# Revit family: 36-52-116 DN65-300
name_source: partatom
category: Pipe Accessories
units: mm (PartAtom-declared; Revit-internal decimal feet)

## family parameters
Always vertical = No
Cut with Voids When Loaded = No
Part Type = Valve - Breaks Into
Round Connector Dimension = Use Diameter
Shared = No
Work Plane-Based = No

## types (13) — shared parameters
2 = 2 mm  [stored 0.00656168 ft]
36-075-52-161086 = DN065_D075
36-090-52-16108699 = DN080_D090
36-110-52-16108699 = DN100_D110
36-125-52-16108699 = DN125_D125
36-140-52-16108699 = DN125_D140
36-160-52-16108699 = DN150_D160
36-180-52-16108699 = DN150_D180
36-200-52-16108699 = DN200_D200
36-225-52-16108699 = DN200_D225
36-250-52-161086 = DN250_D250
36-280-52-161086 = DN250_D280
36-315-52-161086 = DN300_D315
36-400-52-161086 = DN300_D355
Description_ = AVK GATE VALVE, PREMIUM 100, PE PIPE ENDS, PN16
Search_table = 36-52-116 DN65-300
Thickness = 9 mm  [stored 0.0295276 ft]
URL product pages = https://www.avkvalves.com
zero-valued in all types: Default Elevation

## per-type parameters (varying)
- DN065_D075: Body_Height=115 mm; Body_L=54.5 mm; Body_Rib_H=57 mm; Body_Rib_L=85 mm; Body_Rib_Start=28 mm; Body_Rib_T=7 mm  [stored 0.0229659 ft]; Body_W=37 mm; Body_dim=26.4 mm; Body_dim3=59.95 mm; Body_dim4=40.7 mm; Body_dimension1=21.6 mm  [stored 0.0708661 ft]; Body_dimension2=39.1 mm; Bonnet_Dim4=29.9 mm; Bonnet_FL_L=67.5 mm; Bonnet_FL_T=8 mm  [stored 0.0262467 ft]; Bonnet_FL_W=50 mm; Bonnet_dim1=62.68 mm; Bonnet_dim2=29.6 mm; Bonnet_dim3=20.72 mm  [stored 0.067979 ft]; Bonnet_dim4=26.64 mm; Bore=32.5 mm; Bottom_revolve=38.15 mm; D=37.5 mm; DN=65 mm; Dd=32.5 mm; F=17 mm  [stored 0.0557743 ft]; F1=20 mm  [stored 0.0656168 ft]; F2=34 mm; FL_T=18 mm  [stored 0.0590551 ft]; Fillet=24 mm; Fillet1=28.8 mm; Fitting_dim1=24.18 mm; Fitting_dim2=36.26 mm; Fitting_dim3=43.52 mm; Fitting_dim4=45.33 mm; Fitting_mid_L=80.59 mm; Gate valve_Pipe_L=44.4 mm; H=271 mm; H3=322 mm; H3-H=51 mm; L=900 mm; L1=250 mm; OD=93 mm; Raised_R=55 mm; Raised_dis=3 mm  [stored 0.00984252 ft]; Rib1_H=80.5 mm; Rib1_L=25.5 mm; Rib1_W=25.5 mm; Rib2_H=80.5 mm; Rib2_L=25.5 mm; Rib2_W=25.5 mm; Rib3_H=80.5 mm; Rib3_L=15 mm  [stored 0.0492126 ft]; Rib3_W=13.75 mm  [stored 0.0451115 ft]; Rib4_H=80.5 mm; Rib4_L=15 mm  [stored 0.0492126 ft]; Rib4_W=13.75 mm  [stored 0.0451115 ft]; Rib_dim1=18.2 mm  [stored 0.0597113 ft]; Rib_dim2=22.75 mm  [stored 0.0746391 ft]; Rib_t=3.5 mm  [stored 0.0114829 ft]; Stem1=26 mm; Valve_D=41.5 mm; W=76 mm; axis_dim=41.5 mm; body_dim=46.33 mm; cut=5 mm  [stored 0.0164042 ft]; slant=180 mm; stem1=17 mm  [stored 0.0557743 ft]
- DN080_D090: Body_Height=108 mm; Body_L=72 mm; Body_Rib_H=58 mm; Body_Rib_L=85 mm; Body_Rib_Start=28 mm; Body_Rib_T=7.5 mm  [stored 0.0246063 ft]; Body_W=35 mm; Body_dim=30.8 mm; Body_dim3=79.2 mm; Body_dim4=38.5 mm; Body_dimension1=21.6 mm  [stored 0.0708661 ft]; Body_dimension2=40.8 mm; Bonnet_Dim4=29.9 mm; Bonnet_FL_L=85 mm; Bonnet_FL_T=9 mm  [stored 0.0295276 ft]; Bonnet_FL_W=48 mm; Bonnet_dim1=82.8 mm; Bonnet_dim2=28 mm; Bonnet_dim3=19.6 mm  [stored 0.0643045 ft]; Bonnet_dim4=25.2 mm; Bore=40 mm; Bottom_revolve=50.4 mm; D=45 mm; DN=80 mm; Dd=40 mm; F=17 mm  [stored 0.0557743 ft]; F1=20 mm  [stored 0.0656168 ft]; F2=34 mm; FL_T=18 mm  [stored 0.0590551 ft]; Fillet=28 mm; Fillet1=33.6 mm; Fitting_dim1=23.47 mm; Fitting_dim2=35.21 mm; Fitting_dim3=42.25 mm; Fitting_dim4=44.01 mm; Fitting_mid_L=78.24 mm; Gate valve_Pipe_L=42 mm; H=282 mm; H3=342 mm; H3-H=60 mm; L=900 mm; L1=255 mm; OD=100 mm; Raised_R=66 mm; Raised_dis=3 mm  [stored 0.00984252 ft]; Rib1_H=75.6 mm; Rib1_L=29.5 mm; Rib1_W=29.5 mm; Rib2_H=75.6 mm; Rib2_L=29.5 mm; Rib2_W=29.5 mm; Rib3_H=75.6 mm; Rib3_L=15 mm  [stored 0.0492126 ft]; Rib3_W=13.75 mm  [stored 0.0451115 ft]; Rib4_H=75.6 mm; Rib4_L=15 mm  [stored 0.0492126 ft]; Rib4_W=13.75 mm  [stored 0.0451115 ft]; Rib_dim1=22.4 mm  [stored 0.0734908 ft]; Rib_dim2=28 mm; Rib_t=3.75 mm  [stored 0.0123032 ft]; Stem1=26 mm; Valve_D=49 mm; W=85.5 mm; axis_dim=49 mm; body_dim=61.2 mm; cut=5 mm  [stored 0.0164042 ft]; slant=180 mm; stem1=17 mm  [stored 0.0557743 ft]
- DN100_D110: Body_Height=122 mm; Body_L=82 mm; Body_Rib_H=70 mm; Body_Rib_L=85 mm; Body_Rib_Start=28 mm; Body_Rib_T=7.5 mm  [stored 0.0246063 ft]; Body_W=38 mm; Body_dim=35.2 mm; Body_dim3=90.2 mm; Body_dim4=41.8 mm; Body_dimension1=21.6 mm  [stored 0.0708661 ft]; Body_dimension2=44.2 mm; Bonnet_Dim4=32.89 mm; Bonnet_FL_L=96 mm; Bonnet_FL_T=9 mm  [stored 0.0295276 ft]; Bonnet_FL_W=52.5 mm; Bonnet_dim1=94.3 mm; Bonnet_dim2=30.4 mm; Bonnet_dim3=21.28 mm  [stored 0.0698163 ft]; Bonnet_dim4=27.36 mm; Bore=50 mm; Bottom_revolve=57.4 mm; D=55 mm; DN=100 mm; Dd=50 mm; F=19 mm  [stored 0.062336 ft]; F1=22 mm  [stored 0.0721785 ft]; F2=34 mm; FL_T=18 mm  [stored 0.0590551 ft]; Fillet=32 mm; Fillet1=38.4 mm; Fitting_dim1=20.29 mm; Fitting_dim2=30.44 mm; Fitting_dim3=36.53 mm; Fitting_dim4=38.05 mm; Fitting_mid_L=67.65 mm; Gate valve_Pipe_L=45.6 mm; H=305 mm; H3=378 mm; H3-H=73 mm; L=860 mm; L1=250 mm; OD=110 mm; Raised_R=76 mm; Raised_dis=3 mm  [stored 0.00984252 ft]; Rib1_H=85.4 mm; Rib1_L=33.5 mm; Rib1_W=33.5 mm; Rib2_H=85.4 mm; Rib2_L=33.5 mm; Rib2_W=33.5 mm; Rib3_H=85.4 mm; Rib3_L=15 mm  [stored 0.0492126 ft]; Rib3_W=13.75 mm  [stored 0.0451115 ft]; Rib4_H=85.4 mm; Rib4_L=15 mm  [stored 0.0492126 ft]; Rib4_W=13.75 mm  [stored 0.0451115 ft]; Rib_dim1=28 mm; Rib_dim2=35 mm; Rib_t=3.75 mm  [stored 0.0123032 ft]; Stem1=28.6 mm; Valve_D=59 mm; W=96 mm; axis_dim=59 mm; body_dim=69.7 mm; cut=5 mm  [stored 0.0164042 ft]; slant=172 mm; stem1=19 mm  [stored 0.062336 ft]
- DN125_D125: Body_Height=137 mm; Body_L=96.5 mm; Body_Rib_H=85 mm; Body_Rib_L=120 mm; Body_Rib_Start=40 mm; Body_Rib_T=8 mm  [stored 0.0262467 ft]; Body_W=41 mm; Body_dim=37.4 mm; Body_dim3=106.15 mm; Body_dim4=45.1 mm; Body_dimension1=21.6 mm  [stored 0.0708661 ft]; Body_dimension2=46.75 mm; Bonnet_Dim4=32.89 mm; Bonnet_FL_L=110 mm; Bonnet_FL_T=9 mm  [stored 0.0295276 ft]; Bonnet_FL_W=55.5 mm; Bonnet_dim1=110.98 mm; Bonnet_dim2=32.8 mm; Bonnet_dim3=22.96 mm; Bonnet_dim4=29.52 mm; Bore=62.5 mm; Bottom_revolve=67.55 mm; D=62.5 mm; DN=125 mm; Dd=62.5 mm; F=19 mm  [stored 0.062336 ft]; F1=22 mm  [stored 0.0721785 ft]; F2=34 mm; FL_T=18 mm  [stored 0.0590551 ft]; Fillet=34 mm; Fillet1=40.8 mm; Fitting_dim1=10.94 mm; Fitting_dim2=16.41 mm; Fitting_dim3=19.69 mm; Fitting_dim4=20.51 mm; Fitting_mid_L=36.47 mm; Gate valve_Pipe_L=49.2 mm; H=346 mm; H3=432 mm; H3-H=86 mm; L=860 mm; L1=300 mm; OD=125 mm; Raised_R=91 mm; Raised_dis=3 mm  [stored 0.00984252 ft]; Rib1_H=95.9 mm; Rib1_L=35.5 mm; Rib1_W=35.5 mm; Rib2_H=95.9 mm; Rib2_L=35.5 mm; Rib2_W=35.5 mm; Rib3_H=95.9 mm; Rib3_L=15 mm  [stored 0.0492126 ft]; Rib3_W=13.75 mm  [stored 0.0451115 ft]; Rib4_H=95.9 mm; Rib4_L=15 mm  [stored 0.0492126 ft]; Rib4_W=13.75 mm  [stored 0.0451115 ft]; Rib_dim1=35 mm; Rib_dim2=43.75 mm; Rib_t=4 mm  [stored 0.0131234 ft]; Stem1=28.6 mm; Valve_D=71.5 mm; W=110 mm; axis_dim=71.5 mm; body_dim=82.03 mm; cut=0 mm  [stored 0 ft]; slant=172 mm; stem1=19 mm  [stored 0.062336 ft]
- DN125_D140: Body_Height=137 mm; Body_L=96.5 mm; Body_Rib_H=85 mm; Body_Rib_L=120 mm; Body_Rib_Start=40 mm; Body_Rib_T=8 mm  [stored 0.0262467 ft]; Body_W=41 mm; Body_dim=41.8 mm; Body_dim3=106.15 mm; Body_dim4=45.1 mm; Body_dimension1=21.6 mm  [stored 0.0708661 ft]; Body_dimension2=55.25 mm; Bonnet_Dim4=32.89 mm; Bonnet_FL_L=110 mm; Bonnet_FL_T=12 mm  [stored 0.0393701 ft]; Bonnet_FL_W=55.5 mm; Bonnet_dim1=110.98 mm; Bonnet_dim2=32.8 mm; Bonnet_dim3=22.96 mm; Bonnet_dim4=29.52 mm; Bore=62.55 mm; Bottom_revolve=67.55 mm; D=70 mm; DN=125.1 mm; Dd=62.55 mm; F=19 mm  [stored 0.062336 ft]; F1=22 mm  [stored 0.0721785 ft]; F2=34 mm; FL_T=18 mm  [stored 0.0590551 ft]; Fillet=38 mm; Fillet1=45.6 mm; Fitting_dim1=19.24 mm; Fitting_dim2=28.85 mm; Fitting_dim3=34.62 mm; Fitting_dim4=36.07 mm; Fitting_mid_L=64.12 mm; Gate valve_Pipe_L=49.2 mm; H=346 mm; H3=435 mm; H3-H=89 mm; L=860 mm; L1=250 mm; OD=142 mm; Raised_R=105 mm; Raised_dis=3 mm  [stored 0.00984252 ft]; Rib1_H=95.9 mm; Rib1_L=39.5 mm; Rib1_W=39.5 mm; Rib2_H=95.9 mm; Rib2_L=39.5 mm; Rib2_W=39.5 mm; Rib3_H=95.9 mm; Rib3_L=15 mm  [stored 0.0492126 ft]; Rib3_W=13.75 mm  [stored 0.0451115 ft]; Rib4_H=95.9 mm; Rib4_L=15 mm  [stored 0.0492126 ft]; Rib4_W=13.75 mm  [stored 0.0451115 ft]; Rib_dim1=35.03 mm; Rib_dim2=43.79 mm; Rib_t=4 mm  [stored 0.0131234 ft]; Stem1=28.6 mm; Valve_D=71.55 mm; W=136 mm; axis_dim=71.55 mm; body_dim=82.03 mm; cut=7.45 mm  [stored 0.0244423 ft]; slant=172 mm; stem1=19 mm  [stored 0.062336 ft]
- DN150_D160: Body_Height=172 mm; Body_L=122 mm; Body_Rib_H=99 mm; Body_Rib_L=120 mm; Body_Rib_Start=33 mm; Body_Rib_T=9 mm  [stored 0.0295276 ft]; Body_W=48 mm; Body_dim=44 mm; Body_dim3=134.2 mm; Body_dim4=52.8 mm; Body_dimension1=22.8 mm; Body_dimension2=72.25 mm; Bonnet_Dim4=32.89 mm; Bonnet_FL_L=136 mm; Bonnet_FL_T=12 mm  [stored 0.0393701 ft]; Bonnet_FL_W=75 mm; Bonnet_dim1=140.3 mm; Bonnet_dim2=38.4 mm; Bonnet_dim3=26.88 mm; Bonnet_dim4=34.56 mm; Bore=75 mm; Bottom_revolve=85.4 mm; D=80 mm; DN=150 mm; Dd=75 mm; F=19 mm  [stored 0.062336 ft]; F1=22 mm  [stored 0.0721785 ft]; F2=34 mm; FL_T=19 mm  [stored 0.062336 ft]; Fillet=40 mm; Fillet1=48 mm; Fitting_dim1=19.59 mm; Fitting_dim2=29.38 mm; Fitting_dim3=35.26 mm; Fitting_dim4=36.73 mm; Fitting_mid_L=65.29 mm; Gate valve_Pipe_L=57.6 mm; H=400 mm; H3=502 mm; H3-H=102 mm; L=1030 mm; L1=325 mm; OD=170 mm; Raised_R=132 mm; Raised_dis=3 mm  [stored 0.00984252 ft]; Rib1_H=120.4 mm; Rib1_L=41.5 mm; Rib1_W=41.5 mm; Rib2_H=120.4 mm; Rib2_L=41.5 mm; Rib2_W=41.5 mm; Rib3_H=120.4 mm; Rib3_L=15 mm  [stored 0.0492126 ft]; Rib3_W=13.75 mm  [stored 0.0451115 ft]; Rib4_H=120.4 mm; Rib4_L=15 mm  [stored 0.0492126 ft]; Rib4_W=13.75 mm  [stored 0.0451115 ft]; Rib_dim1=42 mm; Rib_dim2=52.5 mm; Rib_t=4.5 mm  [stored 0.0147638 ft]; Stem1=28.6 mm; Valve_D=84 mm; W=166 mm; axis_dim=84 mm; body_dim=103.7 mm; cut=5 mm  [stored 0.0164042 ft]; slant=206 mm; stem1=19 mm  [stored 0.062336 ft]
- DN150_D180: Body_Height=172 mm; Body_L=122 mm; Body_Rib_H=99 mm; Body_Rib_L=120 mm; Body_Rib_Start=33 mm; Body_Rib_T=9 mm  [stored 0.0295276 ft]; Body_W=48 mm; Body_dim=44 mm; Body_dim3=134.2 mm; Body_dim4=52.8 mm; Body_dimension1=22.8 mm; Body_dimension2=72.25 mm; Bonnet_Dim4=32.89 mm; Bonnet_FL_L=136 mm; Bonnet_FL_T=12 mm  [stored 0.0393701 ft]; Bonnet_FL_W=75 mm; Bonnet_dim1=140.3 mm; Bonnet_dim2=38.4 mm; Bonnet_dim3=26.88 mm; Bonnet_dim4=34.56 mm; Bore=75.05 mm; Bottom_revolve=85.4 mm; D=90 mm; DN=150.1 mm; Dd=75 mm; F=19 mm  [stored 0.062336 ft]; F1=22 mm  [stored 0.0721785 ft]; F2=34 mm; FL_T=19 mm  [stored 0.062336 ft]; Fillet=40 mm; Fillet1=48 mm; Fitting_dim1=30.18 mm; Fitting_dim2=45.26 mm; Fitting_dim3=54.32 mm; Fitting_dim4=56.58 mm; Fitting_mid_L=100.59 mm; Gate valve_Pipe_L=57.6 mm; H=400 mm; H3=508 mm; H3-H=108 mm; L=1030 mm; L1=265 mm; OD=170 mm; Raised_R=132 mm; Raised_dis=3 mm  [stored 0.00984252 ft]; Rib1_H=120.4 mm; Rib1_L=41.5 mm; Rib1_W=41.5 mm; Rib2_H=120.4 mm; Rib2_L=41.5 mm; Rib2_W=41.5 mm; Rib3_H=120.4 mm; Rib3_L=15 mm  [stored 0.0492126 ft]; Rib3_W=13.75 mm  [stored 0.0451115 ft]; Rib4_H=120.4 mm; Rib4_L=15 mm  [stored 0.0492126 ft]; Rib4_W=13.75 mm  [stored 0.0451115 ft]; Rib_dim1=42 mm; Rib_dim2=52.5 mm; Rib_t=4.5 mm  [stored 0.0147638 ft]; Stem1=28.6 mm; Valve_D=84 mm; W=166 mm; axis_dim=84 mm; body_dim=103.7 mm; cut=15 mm  [stored 0.0492126 ft]; slant=206 mm; stem1=19 mm  [stored 0.062336 ft]
- DN200_D200: Body_Height=220 mm; Body_L=157 mm; Body_Rib_H=125 mm; Body_Rib_L=140 mm; Body_Rib_Start=52 mm; Body_Rib_T=10 mm  [stored 0.0328084 ft]; Body_W=55 mm; Body_dim=47.3 mm; Body_dim3=172.7 mm; Body_dim4=60.5 mm; Body_dimension1=22.8 mm; Body_dimension2=90.95 mm; Bonnet_Dim4=40.37 mm; Bonnet_FL_L=166 mm; Bonnet_FL_T=12 mm  [stored 0.0393701 ft]; Bonnet_FL_W=85 mm; Bonnet_dim1=180.55 mm; Bonnet_dim2=44 mm; Bonnet_dim3=30.8 mm; Bonnet_dim4=39.6 mm; Bore=100 mm; Bottom_revolve=109.9 mm; D=100 mm; DN=200 mm; Dd=100 mm; F=24 mm; F1=27 mm; F2=34 mm; FL_T=19 mm  [stored 0.062336 ft]; Fillet=43 mm; Fillet1=51.6 mm; Fitting_dim1=35.12 mm; Fitting_dim2=52.68 mm; Fitting_dim3=63.21 mm; Fitting_dim4=65.85 mm; Fitting_mid_L=117.06 mm; Gate valve_Pipe_L=66 mm; H=490 mm; H3=615 mm; H3-H=125 mm; L=1080 mm; L1=255 mm; OD=200 mm; Raised_R=145 mm; Raised_dis=3 mm  [stored 0.00984252 ft]; Rib1_H=154 mm; Rib1_L=44.5 mm; Rib1_W=44.5 mm; Rib2_H=154 mm; Rib2_L=44.5 mm; Rib2_W=44.5 mm; Rib3_H=154 mm; Rib3_L=15 mm  [stored 0.0492126 ft]; Rib3_W=13.75 mm  [stored 0.0451115 ft]; Rib4_H=154 mm; Rib4_L=15 mm  [stored 0.0492126 ft]; Rib4_W=13.75 mm  [stored 0.0451115 ft]; Rib_dim1=56 mm; Rib_dim2=70 mm; Rib_t=5 mm  [stored 0.0164042 ft]; Stem1=35.1 mm; Valve_D=109 mm; W=210 mm; axis_dim=109 mm; body_dim=133.45 mm; cut=0 mm  [stored 0 ft]; slant=216 mm; stem1=24 mm
- DN200_D225: Body_Height=220 mm; Body_L=157 mm; Body_Rib_H=125 mm; Body_Rib_L=140 mm; Body_Rib_Start=52 mm; Body_Rib_T=10 mm  [stored 0.0328084 ft]; Body_W=55 mm; Body_dim=47.3 mm; Body_dim3=172.7 mm; Body_dim4=60.5 mm; Body_dimension1=22.8 mm; Body_dimension2=90.95 mm; Bonnet_Dim4=40.37 mm; Bonnet_FL_L=166 mm; Bonnet_FL_T=12 mm  [stored 0.0393701 ft]; Bonnet_FL_W=85 mm; Bonnet_dim1=180.55 mm; Bonnet_dim2=44 mm; Bonnet_dim3=30.8 mm; Bonnet_dim4=39.6 mm; Bore=100.05 mm; Bottom_revolve=109.9 mm; D=112.5 mm; DN=200.1 mm; Dd=100.05 mm; F=24 mm; F1=27 mm; F2=34 mm; FL_T=19 mm  [stored 0.062336 ft]; Fillet=43 mm; Fillet1=51.6 mm; Fitting_dim1=33.35 mm; Fitting_dim2=50.03 mm; Fitting_dim3=60.04 mm; Fitting_dim4=62.54 mm; Fitting_mid_L=111.18 mm; Gate valve_Pipe_L=66 mm; H=490 mm; H3=632 mm; H3-H=142 mm; L=1080 mm; L1=265 mm; OD=200 mm; Raised_R=145 mm; Raised_dis=3 mm  [stored 0.00984252 ft]; Rib1_H=154 mm; Rib1_L=44.5 mm; Rib1_W=44.5 mm; Rib2_H=154 mm; Rib2_L=44.5 mm; Rib2_W=44.5 mm; Rib3_H=154 mm; Rib3_L=15 mm  [stored 0.0492126 ft]; Rib3_W=13.75 mm  [stored 0.0451115 ft]; Rib4_H=154 mm; Rib4_L=15 mm  [stored 0.0492126 ft]; Rib4_W=13.75 mm  [stored 0.0451115 ft]; Rib_dim1=56.03 mm; Rib_dim2=70.04 mm; Rib_t=5 mm  [stored 0.0164042 ft]; Stem1=35.1 mm; Valve_D=109.05 mm; W=210 mm; axis_dim=109.05 mm; body_dim=133.45 mm; cut=12.45 mm  [stored 0.0408465 ft]; slant=216 mm; stem1=24 mm
- DN250_D250: Body_Height=305 mm; Body_L=164 mm; Body_Rib_H=152 mm; Body_Rib_L=140 mm; Body_Rib_Start=50 mm; Body_Rib_T=10 mm  [stored 0.0328084 ft]; Body_W=79 mm; Body_dim=50.6 mm; Body_dim3=180.4 mm; Body_dim4=86.9 mm; Body_dimension1=27.6 mm; Body_dimension2=97.75 mm; Bonnet_Dim4=46.35 mm; Bonnet_FL_L=186 mm; Bonnet_FL_T=14 mm  [stored 0.0459318 ft]; Bonnet_FL_W=100 mm; Bonnet_dim1=188.6 mm; Bonnet_dim2=63.2 mm; Bonnet_dim3=44.24 mm; Bonnet_dim4=56.88 mm; Bore=125 mm; Bottom_revolve=114.8 mm; D=125 mm; DN=250 mm; Dd=125 mm; F=27 mm; F1=31 mm; F2=47 mm; FL_T=23 mm; Fillet=40 mm; Fillet1=48 mm; Fitting_dim1=18.35 mm; Fitting_dim2=27.53 mm; Fitting_dim3=33.04 mm; Fitting_dim4=34.41 mm; Fitting_mid_L=61.18 mm; Gate valve_Pipe_L=94.8 mm; H=664 mm; H3=810 mm; H3-H=146 mm; L=1280 mm; L1=420 mm; OD=225 mm; Raised_R=183 mm; Raised_dis=3 mm  [stored 0.00984252 ft]; Rib1_H=105 mm; Rib1_L=172 mm; Rib1_W=90 mm; Rib2_H=100 mm; Rib2_L=41 mm; Rib2_W=41 mm; Rib3_H=100 mm; Rib3_L=75 mm; Rib3_W=30 mm; Rib4_H=100 mm; Rib4_L=75 mm; Rib4_W=30 mm; Rib_dim1=70 mm; Rib_dim2=87.5 mm; Rib_t=5 mm  [stored 0.0164042 ft]; Stem1=40.3 mm; Valve_D=134 mm; W=224 mm; axis_dim=134 mm; body_dim=139.4 mm; cut=0 mm  [stored 0 ft]; slant=256 mm; stem1=27 mm
- DN250_D280: Body_Height=305 mm; Body_L=164 mm; Body_Rib_H=152 mm; Body_Rib_L=140 mm; Body_Rib_Start=50 mm; Body_Rib_T=10 mm  [stored 0.0328084 ft]; Body_W=79 mm; Body_dim=50.6 mm; Body_dim3=180.4 mm; Body_dim4=86.9 mm; Body_dimension1=27.6 mm; Body_dimension2=97.75 mm; Bonnet_Dim4=46.35 mm; Bonnet_FL_L=186 mm; Bonnet_FL_T=14 mm  [stored 0.0459318 ft]; Bonnet_FL_W=100 mm; Bonnet_dim1=188.6 mm; Bonnet_dim2=63.2 mm; Bonnet_dim3=44.24 mm; Bonnet_dim4=56.88 mm; Bore=125.05 mm; Bottom_revolve=114.8 mm; D=140 mm; DN=250.1 mm; Dd=125.05 mm; F=27 mm; F1=31 mm; F2=47 mm; FL_T=23 mm; Fillet=40 mm; Fillet1=48 mm; Fitting_dim1=35.12 mm; Fitting_dim2=52.68 mm; Fitting_dim3=63.21 mm; Fitting_dim4=65.85 mm; Fitting_mid_L=117.06 mm; Gate valve_Pipe_L=94.8 mm; H=664 mm; H3=823 mm; H3-H=159 mm; L=1360 mm; L1=365 mm; OD=225 mm; Raised_R=183 mm; Raised_dis=3 mm  [stored 0.00984252 ft]; Rib1_H=105 mm; Rib1_L=172 mm; Rib1_W=90 mm; Rib2_H=100 mm; Rib2_L=41 mm; Rib2_W=41 mm; Rib3_H=100 mm; Rib3_L=75 mm; Rib3_W=30 mm; Rib4_H=100 mm; Rib4_L=75 mm; Rib4_W=30 mm; Rib_dim1=70.03 mm; Rib_dim2=87.54 mm; Rib_t=5 mm  [stored 0.0164042 ft]; Stem1=40.3 mm; Valve_D=134.05 mm; W=224 mm; axis_dim=134.05 mm; body_dim=139.4 mm; cut=14.95 mm  [stored 0.0490486 ft]; slant=272 mm; stem1=27 mm
- DN300_D315: Body_Height=370 mm; Body_L=206 mm; Body_Rib_H=193 mm; Body_Rib_L=191 mm; Body_Rib_Start=57 mm; Body_Rib_T=20 mm  [stored 0.0656168 ft]; Body_W=108.5 mm; Body_dim=50.6 mm; Body_dim3=226.6 mm; Body_dim4=119.35 mm; Body_dimension1=31.2 mm; Body_dimension2=131.75 mm; Bonnet_Dim4=46.35 mm; Bonnet_FL_L=224 mm; Bonnet_FL_T=14 mm  [stored 0.0459318 ft]; Bonnet_FL_W=125 mm; Bonnet_dim1=236.9 mm; Bonnet_dim2=86.8 mm; Bonnet_dim3=60.76 mm; Bonnet_dim4=78.12 mm; Bore=150 mm; Bottom_revolve=144.2 mm; D=157.5 mm; DN=300 mm; Dd=150 mm; F=27 mm; F1=31 mm; F2=47 mm; FL_T=26 mm; Fillet=46 mm; Fillet1=55.2 mm; Fitting_dim1=36.44 mm; Fitting_dim2=54.66 mm; Fitting_dim3=65.59 mm; Fitting_dim4=68.33 mm; Fitting_mid_L=121.47 mm; Gate valve_Pipe_L=130.2 mm; H=740 mm; H3=924 mm; H3-H=184 mm; L=1420 mm; L1=355 mm; OD=260 mm; Raised_R=215 mm; Raised_dis=4 mm  [stored 0.0131234 ft]; Rib1_H=125 mm; Rib1_L=214 mm; Rib1_W=115 mm; Rib2_H=280 mm; Rib2_L=214 mm; Rib2_W=115 mm; Rib3_H=100 mm; Rib3_L=75 mm; Rib3_W=30 mm; Rib4_H=120 mm; Rib4_L=75 mm; Rib4_W=30 mm; Rib_dim1=84 mm; Rib_dim2=105 mm; Rib_t=10 mm  [stored 0.0328084 ft]; Stem1=40.3 mm; Valve_D=159 mm; W=274 mm; axis_dim=159 mm; body_dim=175.1 mm; cut=7.5 mm  [stored 0.0246063 ft]; slant=284 mm; stem1=27 mm
- DN300_D355: Body_Height=370 mm; Body_L=206 mm; Body_Rib_H=193 mm; Body_Rib_L=191 mm; Body_Rib_Start=57 mm; Body_Rib_T=20 mm  [stored 0.0656168 ft]; Body_W=108.5 mm; Body_dim=50.6 mm; Body_dim3=226.6 mm; Body_dim4=119.35 mm; Body_dimension1=31.2 mm; Body_dimension2=131.75 mm; Bonnet_Dim4=46.35 mm; Bonnet_FL_L=224 mm; Bonnet_FL_T=14 mm  [stored 0.0459318 ft]; Bonnet_FL_W=125 mm; Bonnet_dim1=236.9 mm; Bonnet_dim2=86.8 mm; Bonnet_dim3=60.76 mm; Bonnet_dim4=78.12 mm; Bore=150.05 mm; Bottom_revolve=144.2 mm; D=177.5 mm; DN=300.1 mm; Dd=150.05 mm; F=27 mm; F1=31 mm; F2=47 mm; FL_T=26 mm; Fillet=46 mm; Fillet1=55.2 mm; Fitting_dim1=45.26 mm; Fitting_dim2=67.9 mm; Fitting_dim3=81.48 mm; Fitting_dim4=84.87 mm; Fitting_mid_L=150.88 mm; Gate valve_Pipe_L=130.2 mm; H=740 mm; H3=961 mm; H3-H=221 mm; L=1520 mm; L1=355 mm; OD=260 mm; Raised_R=215 mm; Raised_dis=4 mm  [stored 0.0131234 ft]; Rib1_H=125 mm; Rib1_L=214 mm; Rib1_W=115 mm; Rib2_H=280 mm; Rib2_L=214 mm; Rib2_W=115 mm; Rib3_H=100 mm; Rib3_L=75 mm; Rib3_W=30 mm; Rib4_H=120 mm; Rib4_L=75 mm; Rib4_W=30 mm; Rib_dim1=84.03 mm; Rib_dim2=105.04 mm; Rib_t=10 mm  [stored 0.0328084 ft]; Stem1=40.3 mm; Valve_D=159.05 mm; W=274 mm; axis_dim=159.05 mm; body_dim=175.1 mm; cut=27.45 mm; slant=304 mm; stem1=27 mm

note: [stored X ft] marks values corroborated as IEEE doubles in the binary element streams (Revit-internal decimal feet)

## geometry (parser evidence)
native form markers: Sweep x17
no freeform markers — native parametric forms only
